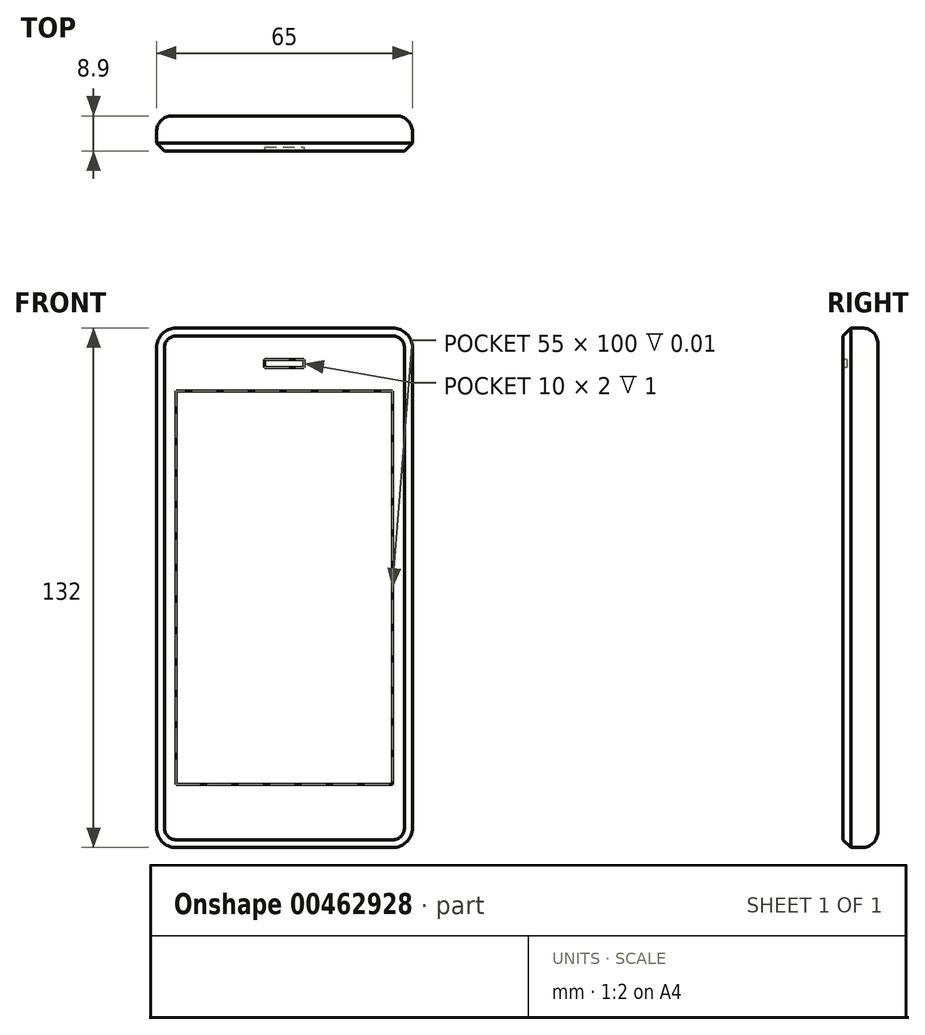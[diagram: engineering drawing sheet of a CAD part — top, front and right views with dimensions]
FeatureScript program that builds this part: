
annotation { "Feature Type Name" : "Feature", "Feature Type Description" : "" }
export const myFeature = defineFeature(function(context is Context, id is Id, definition is map)
    precondition{}
    {
        {
            var Q0;
            Q0=qCreatedBy(makeId("Front.planeOp"),FACE);
            var sketch = newSketch(context, id + "F0", { "sketchPlane" : qUnion([Q0])});
            skLineSegment(sketch, "E0.bottom", {"start": v(32.5, -66) * mm, "end": v(-32.5, -66) * mm});
            skLineSegment(sketch, "E0.top", {"start": v(32.5, 66) * mm, "end": v(-32.5, 66) * mm});
            skLineSegment(sketch, "E0.left", {"start": v(32.5, -66) * mm, "end": v(32.5, 66) * mm});
            skLineSegment(sketch, "E0.right", {"start": v(-32.5, -66) * mm, "end": v(-32.5, 66) * mm});
            skPoint(sketch, "E0.middle", {"position": v(0, 0) * mm});
            skSolve(sketch);
        }
        {
            var Q0;
            Q0 = qSketchRegion(id + "F0", true);
            extrude(context, id + "F1", {"entities" : qUnion([Q0]), "depth" : 8.9 * mm});
        }
        {
            var Q0;
            Q0=makeQuery(id+"F1.opExtrude","SWEPT_EDGE",EDGE,{"disambiguationData":[OSD([sQuery(id+"F0.wireOp",EDGE,"E0.top"),sQuery(id+"F0.wireOp",EDGE,"E0.right")])]});
            var Q1;
            Q1=makeQuery(id+"F1.opExtrude","SWEPT_EDGE",EDGE,{"disambiguationData":[OSD([sQuery(id+"F0.wireOp",EDGE,"E0.top"),sQuery(id+"F0.wireOp",EDGE,"E0.left")])]});
            var Q2;
            Q2=makeQuery(id+"F1.opExtrude","SWEPT_EDGE",EDGE,{"disambiguationData":[OSD([sQuery(id+"F0.wireOp",EDGE,"E0.bottom"),sQuery(id+"F0.wireOp",EDGE,"E0.left")])]});
            var Q3;
            Q3=makeQuery(id+"F1.opExtrude","SWEPT_EDGE",EDGE,{"disambiguationData":[OSD([sQuery(id+"F0.wireOp",EDGE,"E0.bottom"),sQuery(id+"F0.wireOp",EDGE,"E0.right")])]});
            fillet(context, id + "F2", {"entities" : qUnion([Q0, Q1, Q2, Q3]), "radius" : 5 * mm, "tangentPropagation" : true, "allowEdgeOverflow" : false});
        }
        {
            var Q0;
            Q0=makeQuery(id+"F1.opExtrude","CAP_EDGE",EDGE,{"disambiguationData":[OSD([sQuery(id+"F0.wireOp",EDGE,"E0.left")])],"isStart":true});
            fillet(context, id + "F3", {"entities" : qUnion([Q0]), "radius" : 4 * mm, "tangentPropagation" : true, "allowEdgeOverflow" : false});
        }
        {
            var Q0;
            Q0=makeQuery(id+"F1.opExtrude","CAP_EDGE",EDGE,{"disambiguationData":[OSD([sQuery(id+"F0.wireOp",EDGE,"E0.left")])],"isStart":false});
            chamfer(context, id + "F4", {"entities" : qUnion([Q0]), "width" : 2 * mm, "tangentPropagation" : true});
        }
        {
            var Q0;
            Q0=makeQuery(id+"F1.opExtrude","CAP_FACE",FACE,{"disambiguationData":[OSD([sQuery(id+"F0.wireOp",EDGE,"E0.bottom"),sQuery(id+"F0.wireOp",EDGE,"E0.top"),sQuery(id+"F0.wireOp",EDGE,"E0.left"),sQuery(id+"F0.wireOp",EDGE,"E0.right")])],"isStart":false});
            var sketch = newSketch(context, id + "F5", { "sketchPlane" : qUnion([Q0])});
            skSolve(sketch);
        }
        {
            var Q0;
            {var subQ0=sQuery(id+"F0.wireOp",EDGE,"E0.right");var subQ1=sQuery(id+"F0.wireOp",EDGE,"E0.left");var subQ2=sQuery(id+"F0.wireOp",EDGE,"E0.top");var subQ3=sQuery(id+"F0.wireOp",EDGE,"E0.bottom");var subQ4=makeQuery(id+"F1.opExtrude","CAP_FACE",FACE,{"disambiguationData":[OSD([subQ3,subQ2,subQ1,subQ0])],"isStart":false});var subQ5=subQ4;Q0=makeQuery(id+"F5.imprint","IMPRINT",FACE,{"disambiguationData":[TD([[makeQuery(id+"F5.imprint","IMPRINT",EDGE,{"derivedFrom":makeQuery(id+"F4.opChamfer","BLEND_EDGE",EDGE,{"blendedFrom":[makeQuery(id+"F1.opExtrude","CAP_EDGE",EDGE,{"disambiguationData":[OSD([subQ3])],"isStart":false}),subQ5],"blendedInto":[subQ5]})}),1.0]])]});}
            var sketch = newSketch(context, id + "F6", { "sketchPlane" : qUnion([Q0])});
            skLineSegment(sketch, "E1.bottom", {"start": v(27.5, -50) * mm, "end": v(-27.5, -50) * mm});
            skLineSegment(sketch, "E1.top", {"start": v(27.5, 50) * mm, "end": v(-27.5, 50) * mm});
            skLineSegment(sketch, "E1.left", {"start": v(27.5, -50) * mm, "end": v(27.5, 50) * mm});
            skLineSegment(sketch, "E1.right", {"start": v(-27.5, -50) * mm, "end": v(-27.5, 50) * mm});
            skPoint(sketch, "E1.middle", {"position": v(0, 0) * mm});
            skSolve(sketch);
        }
        {
            var Q0;
            Q0 = qSketchRegion(id + "F6", true);
            extrude(context, id + "F7", {"entities" : qUnion([Q0]), "operationType" : NewBodyOperationType.REMOVE, "oppositeDirection" : true, "depth" : 0.01 * mm});
        }
        {
            var Q0;
            {var subQ0=sQuery(id+"F0.wireOp",EDGE,"E0.right");var subQ1=sQuery(id+"F0.wireOp",EDGE,"E0.left");var subQ2=sQuery(id+"F0.wireOp",EDGE,"E0.top");var subQ3=sQuery(id+"F0.wireOp",EDGE,"E0.bottom");var subQ4=makeQuery(id+"F1.opExtrude","CAP_FACE",FACE,{"disambiguationData":[OSD([subQ3,subQ2,subQ1,subQ0])],"isStart":false});var subQ5=subQ4;Q0=makeQuery(id+"F5.imprint","IMPRINT",FACE,{"disambiguationData":[TD([[makeQuery(id+"F5.imprint","IMPRINT",EDGE,{"derivedFrom":makeQuery(id+"F4.opChamfer","BLEND_EDGE",EDGE,{"blendedFrom":[makeQuery(id+"F1.opExtrude","CAP_EDGE",EDGE,{"disambiguationData":[OSD([subQ3])],"isStart":false}),subQ5],"blendedInto":[subQ5]})}),1.0]])]});}
            var sketch = newSketch(context, id + "F8", { "sketchPlane" : qUnion([Q0])});
            skLineSegment(sketch, "E2.bottom", {"start": v(-5, 58) * mm, "end": v(5, 58) * mm});
            skLineSegment(sketch, "E2.top", {"start": v(-5, 56) * mm, "end": v(5, 56) * mm});
            skLineSegment(sketch, "E2.left", {"start": v(-5, 58) * mm, "end": v(-5, 56) * mm});
            skLineSegment(sketch, "E2.right", {"start": v(5, 58) * mm, "end": v(5, 56) * mm});
            skSolve(sketch);
        }
        {
            var Q0;
            Q0 = qSketchRegion(id + "F8", true);
            extrude(context, id + "F9", {"entities" : qUnion([Q0]), "operationType" : NewBodyOperationType.REMOVE, "oppositeDirection" : true, "depth" : 1 * mm});
        }
    });
